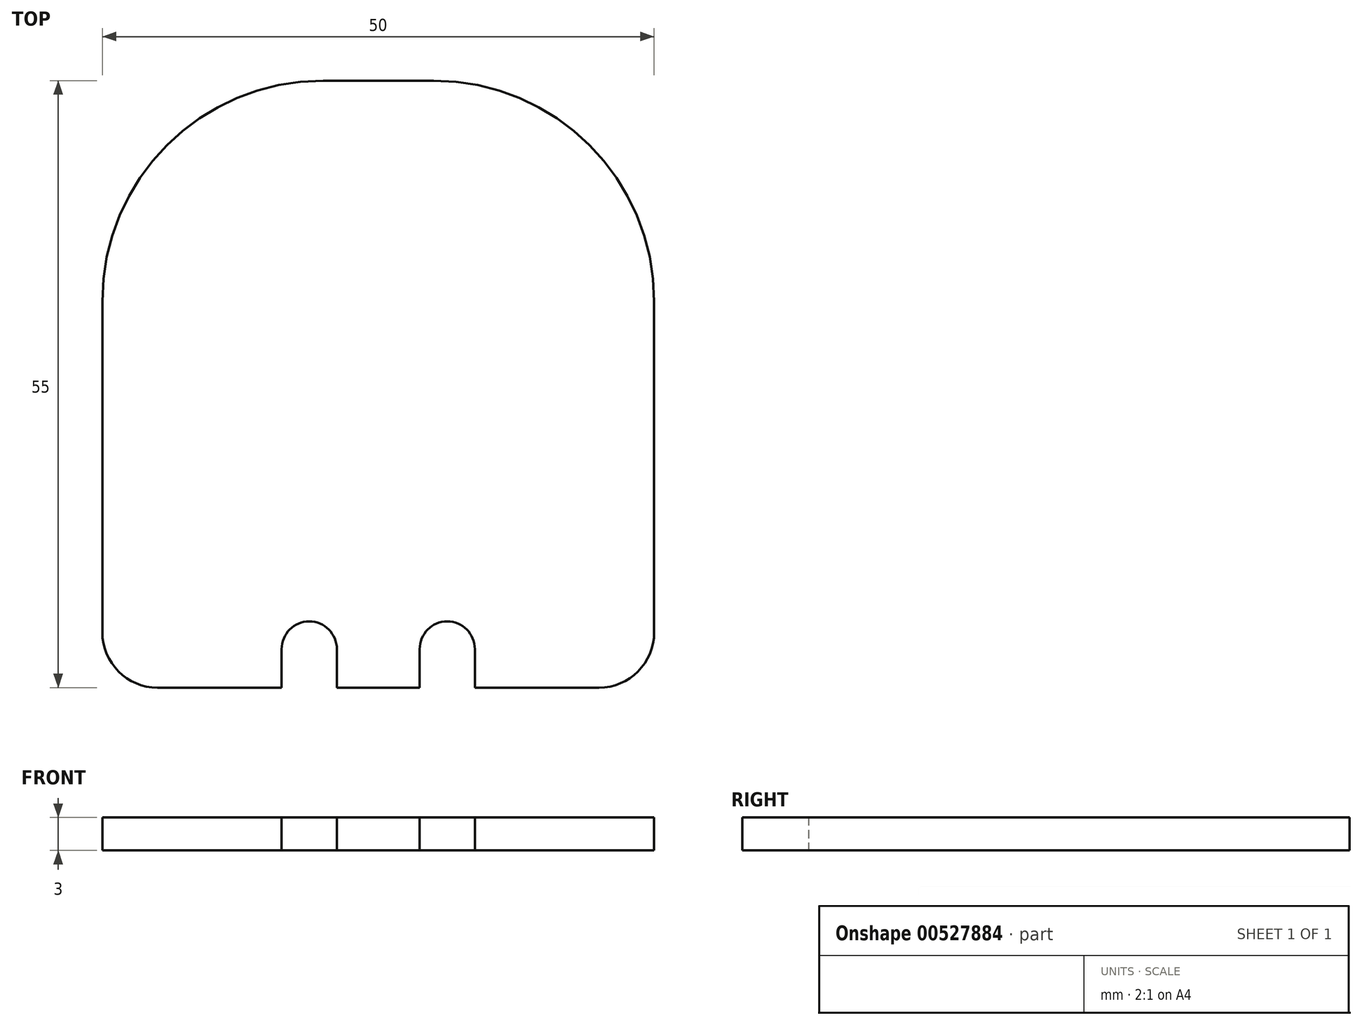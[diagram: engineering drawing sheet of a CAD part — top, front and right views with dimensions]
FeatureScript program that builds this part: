
annotation { "Feature Type Name" : "Feature", "Feature Type Description" : "" }
export const myFeature = defineFeature(function(context is Context, id is Id, definition is map)
    precondition{}
    {
        {
            var Q0;
            Q0=qCreatedBy(makeId("Top.planeOp"),FACE);
            var sketch = newSketch(context, id + "F0", { "sketchPlane" : qUnion([Q0])});
            skLineSegment(sketch, "E0.bottom", {"start": v(-5, 27.5) * mm, "end": v(5, 27.5) * mm});
            skLineSegment(sketch, "E0.top", {"start": v(-20, -27.5) * mm, "end": v(20, -27.5) * mm});
            skLineSegment(sketch, "E0.left", {"start": v(-25, 7.5) * mm, "end": v(-25, -22.5) * mm});
            skLineSegment(sketch, "E0.right", {"start": v(25, 7.5) * mm, "end": v(25, -22.5) * mm});
            skPoint(sketch, "E0.middle", {"position": v(0, 0) * mm});
            skPoint(sketch, "E1.visualSharp", {"position": v(-25, 27.5) * mm});
            skArc(sketch, "E1.filletArc", {"start": v(-5, 27.5) * mm, "mid": v(-19.14, 21.64) * mm, "end": v(-25, 7.5) * mm});
            skPoint(sketch, "E2.visualSharp", {"position": v(25, 27.5) * mm});
            skArc(sketch, "E2.filletArc", {"start": v(25, 7.5) * mm, "mid": v(19.14, 21.64) * mm, "end": v(5, 27.5) * mm});
            skPoint(sketch, "E3.visualSharp", {"position": v(-25, -27.5) * mm});
            skArc(sketch, "E3.filletArc", {"start": v(-25, -22.5) * mm, "mid": v(-23.54, -26.04) * mm, "end": v(-20, -27.5) * mm});
            skPoint(sketch, "E4.visualSharp", {"position": v(25, -27.5) * mm});
            skArc(sketch, "E4.filletArc", {"start": v(20, -27.5) * mm, "mid": v(23.54, -26.04) * mm, "end": v(25, -22.5) * mm});
            skCircle(sketch, "E5", {"center": v(-6.25, -24) * mm, "radius": 2.5 * mm});
            skCircle(sketch, "E6.MirrorC", {"center": v(6.25, -24) * mm, "radius": 2.5 * mm});
            skLineSegment(sketch, "E7", {"start": v(-8.75, -24) * mm, "end": v(-8.75, -27.5) * mm});
            skLineSegment(sketch, "E8", {"start": v(-3.75, -24) * mm, "end": v(-3.75, -27.5) * mm});
            skLineSegment(sketch, "E9", {"start": v(3.75, -24) * mm, "end": v(3.75, -27.5) * mm});
            skLineSegment(sketch, "E10", {"start": v(8.75, -24) * mm, "end": v(8.75, -27.5) * mm});
            skSolve(sketch);
        }
        {
            var Q0;
            Q0=makeQuery(id+"F0.imprint","IMPRINT",FACE,{"disambiguationData":[TD([[makeQuery(id+"F0.imprint","IMPRINT",EDGE,{"derivedFrom":sQuery(id+"F0.wireOp",EDGE,"E0.bottom")}),-1.0]])]});
            extrude(context, id + "F1", {"entities" : qUnion([Q0]), "depth" : 3 * mm, "offsetDistance" : 25 * mm});
        }
    });
